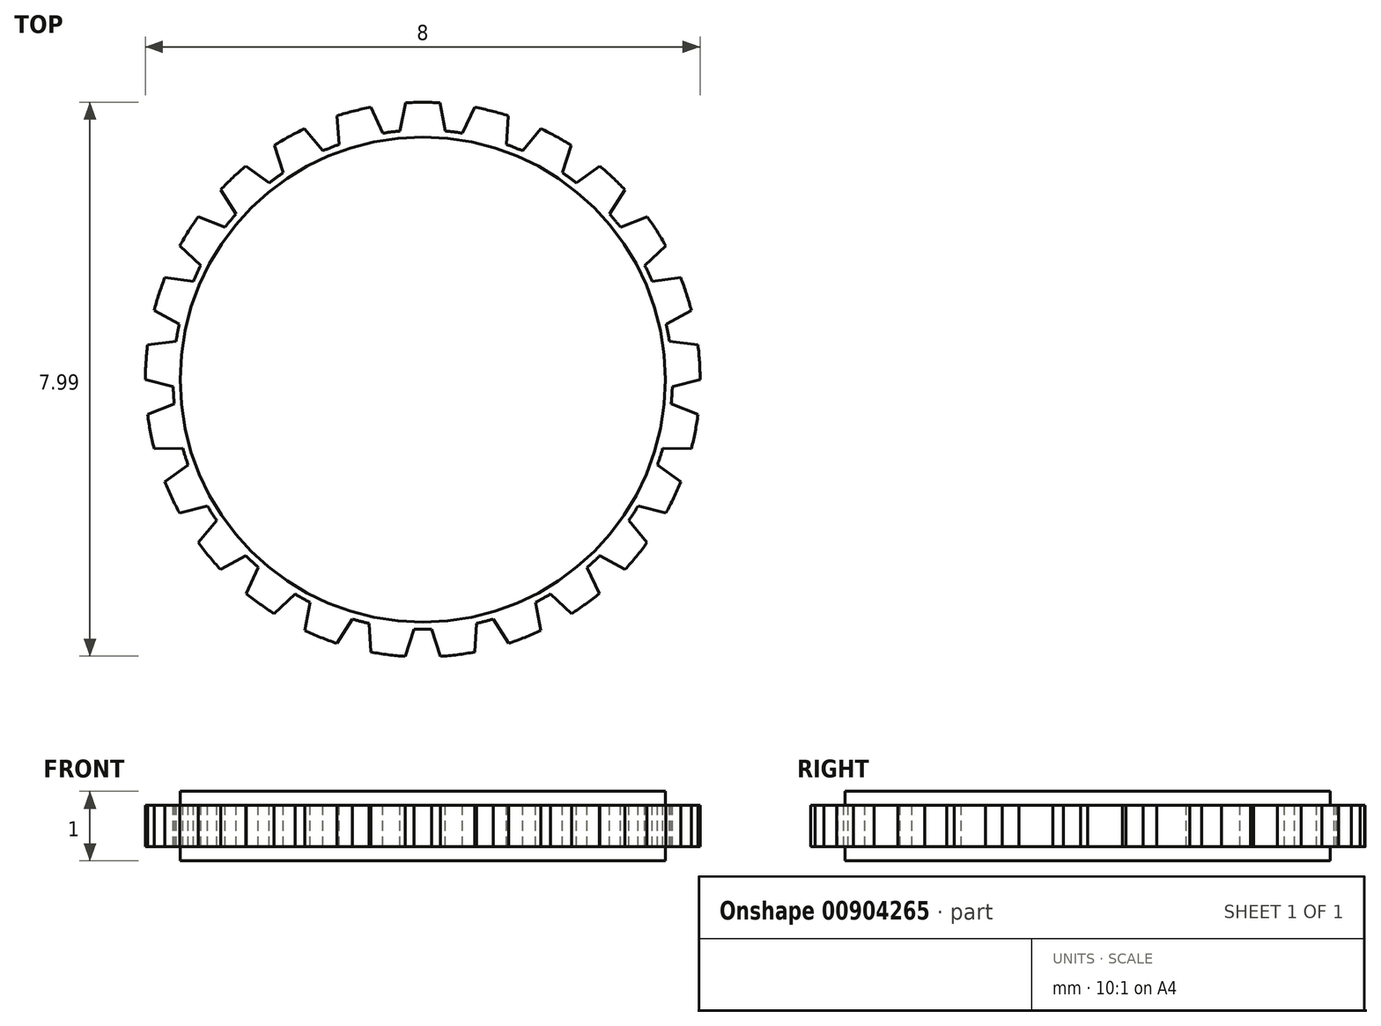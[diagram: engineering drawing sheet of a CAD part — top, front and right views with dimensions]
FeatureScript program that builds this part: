
annotation { "Feature Type Name" : "Feature", "Feature Type Description" : "" }
export const myFeature = defineFeature(function(context is Context, id is Id, definition is map)
    precondition{}
    {
        {
            var Q0;
            Q0=qCreatedBy(makeId("Front.planeOp"),FACE);
            var sketch = newSketch(context, id + "F0", { "sketchPlane" : qUnion([Q0])});
            skLineSegment(sketch, "E0.bottom", {"start": v(0, 0) * mm, "end": v(-4, 0) * mm});
            skLineSegment(sketch, "E0.top", {"start": v(0, 1) * mm, "end": v(-4, 1) * mm});
            skLineSegment(sketch, "E0.left", {"start": v(0, 0) * mm, "end": v(0, 1) * mm});
            skLineSegment(sketch, "E0.right", {"start": v(-4, 0) * mm, "end": v(-4, 1) * mm});
            skLineSegment(sketch, "E1.bottom", {"start": v(0, 1) * mm, "end": v(-1, 1) * mm});
            skLineSegment(sketch, "E1.top", {"start": v(0, 0) * mm, "end": v(-1, 0) * mm});
            skLineSegment(sketch, "E1.left", {"start": v(0, 1) * mm, "end": v(0, 0) * mm});
            skLineSegment(sketch, "E1.right", {"start": v(-1, 1) * mm, "end": v(-1, 0) * mm});
            skSolve(sketch);
        }
        {
            var Q0;
            Q0=makeQuery(id+"F0.imprint","IMPRINT",FACE,{"disambiguationData":[TD([[makeQuery(id+"F0.imprint","IMPRINT",EDGE,{"derivedFrom":sQuery(id+"F0.wireOp",EDGE,"E0.bottom")}),-1.0]])]});
            var Q1;
            Q1=sQuery(id+"F0.wireOp",EDGE,"E1.left");
            revolve(context, id + "F1", {"surfaceOperationType" : NewSurfaceOperationType.NEW, "entities" : qUnion([Q0]), "axis" : qUnion([Q1]), "revolveType" : RevolveType.FULL});
        }
        {
            var Q0;
            Q0=makeQuery(id+"F1.opRevolve","SWEPT_FACE",FACE,{"disambiguationData":[OSD([sQuery(id+"F0.wireOp",EDGE,"E0.top")])]});
            var sketch = newSketch(context, id + "F2", { "sketchPlane" : qUnion([Q0])});
            skLineSegment(sketch, "E2", {"start": v(0, 0) * mm, "end": v(-0.25, 4) * mm});
            skLineSegment(sketch, "E3", {"start": v(0, 0) * mm, "end": v(0.25, 4) * mm});
            skLineSegment(sketch, "E4.1.0", {"start": v(0, 0) * mm, "end": v(-1.23, 3.8) * mm});
            skLineSegment(sketch, "E4.1.1", {"start": v(0, 0) * mm, "end": v(-0.75, 3.93) * mm});
            skLineSegment(sketch, "E4.2.0", {"start": v(0, 0) * mm, "end": v(-2.14, 3.38) * mm});
            skLineSegment(sketch, "E4.2.1", {"start": v(0, 0) * mm, "end": v(-1.7, 3.62) * mm});
            skPoint(sketch, "E4.center", {"position": v(0, 0) * mm});
            skLineSegment(sketch, "E5.2.3.0", {"start": v(0, 0) * mm, "end": v(-2.92, 2.74) * mm});
            skLineSegment(sketch, "E5.3.3.0", {"start": v(0, 0) * mm, "end": v(-2.55, 3.08) * mm});
            skLineSegment(sketch, "E5.2.4.0", {"start": v(0, 0) * mm, "end": v(-3.5, 1.93) * mm});
            skLineSegment(sketch, "E5.3.4.0", {"start": v(0, 0) * mm, "end": v(-3.24, 2.35) * mm});
            skLineSegment(sketch, "E5.2.5.0", {"start": v(0, 0) * mm, "end": v(-3.87, 1) * mm});
            skLineSegment(sketch, "E5.3.5.0", {"start": v(0, 0) * mm, "end": v(-3.72, 1.47) * mm});
            skLineSegment(sketch, "E5.2.6.0", {"start": v(0, 0) * mm, "end": v(-4, 0) * mm});
            skLineSegment(sketch, "E5.3.6.0", {"start": v(0, 0) * mm, "end": v(-3.97, 0.5) * mm});
            skLineSegment(sketch, "E5.2.7.0", {"start": v(0, 0) * mm, "end": v(-3.87, -1) * mm});
            skLineSegment(sketch, "E5.3.7.0", {"start": v(0, 0) * mm, "end": v(-3.97, -0.5) * mm});
            skLineSegment(sketch, "E5.2.8.0", {"start": v(0, 0) * mm, "end": v(-3.5, -1.93) * mm});
            skLineSegment(sketch, "E5.3.8.0", {"start": v(0, 0) * mm, "end": v(-3.72, -1.47) * mm});
            skLineSegment(sketch, "E5.2.9.0", {"start": v(0, 0) * mm, "end": v(-2.92, -2.74) * mm});
            skLineSegment(sketch, "E5.3.9.0", {"start": v(0, 0) * mm, "end": v(-3.24, -2.35) * mm});
            skLineSegment(sketch, "E5.2.10.0", {"start": v(0, 0) * mm, "end": v(-2.14, -3.38) * mm});
            skLineSegment(sketch, "E5.3.10.0", {"start": v(0, 0) * mm, "end": v(-2.55, -3.08) * mm});
            skLineSegment(sketch, "E5.2.11.0", {"start": v(0, 0) * mm, "end": v(-1.24, -3.8) * mm});
            skLineSegment(sketch, "E5.3.11.0", {"start": v(0, 0) * mm, "end": v(-1.7, -3.62) * mm});
            skLineSegment(sketch, "E5.2.12.0", {"start": v(0, 0) * mm, "end": v(-0.25, -4) * mm});
            skLineSegment(sketch, "E5.3.12.0", {"start": v(0, 0) * mm, "end": v(-0.75, -3.93) * mm});
            skLineSegment(sketch, "E5.2.13.0", {"start": v(0, 0) * mm, "end": v(0.75, -3.93) * mm});
            skLineSegment(sketch, "E5.3.13.0", {"start": v(0, 0) * mm, "end": v(0.25, -4) * mm});
            skLineSegment(sketch, "E5.2.14.0", {"start": v(0, 0) * mm, "end": v(1.7, -3.62) * mm});
            skLineSegment(sketch, "E5.3.14.0", {"start": v(0, 0) * mm, "end": v(1.24, -3.8) * mm});
            skLineSegment(sketch, "E6.2.15.0", {"start": v(0, 0) * mm, "end": v(2.55, -3.08) * mm});
            skLineSegment(sketch, "E6.3.15.0", {"start": v(0, 0) * mm, "end": v(2.14, -3.38) * mm});
            skLineSegment(sketch, "E6.2.16.0", {"start": v(0, 0) * mm, "end": v(3.24, -2.35) * mm});
            skLineSegment(sketch, "E6.3.16.0", {"start": v(0, 0) * mm, "end": v(2.92, -2.74) * mm});
            skLineSegment(sketch, "E6.2.17.0", {"start": v(0, 0) * mm, "end": v(3.72, -1.47) * mm});
            skLineSegment(sketch, "E6.3.17.0", {"start": v(0, 0) * mm, "end": v(3.5, -1.93) * mm});
            skLineSegment(sketch, "E6.2.18.0", {"start": v(0, 0) * mm, "end": v(3.97, -0.5) * mm});
            skLineSegment(sketch, "E6.3.18.0", {"start": v(0, 0) * mm, "end": v(3.87, -1) * mm});
            skLineSegment(sketch, "E6.2.19.0", {"start": v(0, 0) * mm, "end": v(3.97, 0.5) * mm});
            skLineSegment(sketch, "E6.3.19.0", {"start": v(0, 0) * mm, "end": v(4, 0) * mm});
            skLineSegment(sketch, "E7.2.20.0", {"start": v(0, 0) * mm, "end": v(3.72, 1.47) * mm});
            skLineSegment(sketch, "E7.3.20.0", {"start": v(0, 0) * mm, "end": v(3.87, 1) * mm});
            skLineSegment(sketch, "E7.2.21.0", {"start": v(0, 0) * mm, "end": v(3.24, 2.35) * mm});
            skLineSegment(sketch, "E7.3.21.0", {"start": v(0, 0) * mm, "end": v(3.5, 1.93) * mm});
            skLineSegment(sketch, "E7.2.22.0", {"start": v(0, 0) * mm, "end": v(2.55, 3.08) * mm});
            skLineSegment(sketch, "E7.3.22.0", {"start": v(0, 0) * mm, "end": v(2.92, 2.74) * mm});
            skLineSegment(sketch, "E7.2.23.0", {"start": v(0, 0) * mm, "end": v(1.7, 3.62) * mm});
            skLineSegment(sketch, "E7.3.23.0", {"start": v(0, 0) * mm, "end": v(2.14, 3.38) * mm});
            skLineSegment(sketch, "E7.2.24.0", {"start": v(0, 0) * mm, "end": v(0.75, 3.93) * mm});
            skLineSegment(sketch, "E7.3.24.0", {"start": v(0, 0) * mm, "end": v(1.23, 3.8) * mm});
            skCircle(sketch, "E8", {"center": v(0, 0) * mm, "radius": 3.6 * mm});
            skLineSegment(sketch, "E9", {"start": v(-1, 0) * mm, "end": v(-0.25, 4) * mm});
            skLineSegment(sketch, "E10", {"start": v(1, 0) * mm, "end": v(0.25, 4) * mm});
            skLineSegment(sketch, "E11.1.0", {"start": v(0.97, 0.25) * mm, "end": v(-0.75, 3.93) * mm});
            skLineSegment(sketch, "E11.1.1", {"start": v(-0.97, -0.25) * mm, "end": v(-1.23, 3.8) * mm});
            skLineSegment(sketch, "E11.2.0", {"start": v(0.88, 0.48) * mm, "end": v(-1.7, 3.62) * mm});
            skLineSegment(sketch, "E11.2.1", {"start": v(-0.88, -0.48) * mm, "end": v(-2.14, 3.38) * mm});
            skLineSegment(sketch, "E12.1.3.0", {"start": v(0.73, 0.68) * mm, "end": v(-2.55, 3.08) * mm});
            skLineSegment(sketch, "E12.3.3.0", {"start": v(-0.73, -0.68) * mm, "end": v(-2.92, 2.74) * mm});
            skLineSegment(sketch, "E12.1.4.0", {"start": v(0.54, 0.84) * mm, "end": v(-3.24, 2.35) * mm});
            skLineSegment(sketch, "E12.3.4.0", {"start": v(-0.54, -0.84) * mm, "end": v(-3.5, 1.93) * mm});
            skLineSegment(sketch, "E12.1.5.0", {"start": v(0.3, 0.95) * mm, "end": v(-3.72, 1.47) * mm});
            skLineSegment(sketch, "E12.3.5.0", {"start": v(-0.3, -0.95) * mm, "end": v(-3.87, 1) * mm});
            skLineSegment(sketch, "E12.1.6.0", {"start": v(0.06, 1) * mm, "end": v(-3.97, 0.5) * mm});
            skLineSegment(sketch, "E12.3.6.0", {"start": v(-0.06, -1) * mm, "end": v(-4, 0) * mm});
            skLineSegment(sketch, "E12.1.7.0", {"start": v(-0.19, 0.98) * mm, "end": v(-3.97, -0.5) * mm});
            skLineSegment(sketch, "E12.3.7.0", {"start": v(0.19, -0.98) * mm, "end": v(-3.87, -1) * mm});
            skLineSegment(sketch, "E12.1.8.0", {"start": v(-0.43, 0.9) * mm, "end": v(-3.72, -1.47) * mm});
            skLineSegment(sketch, "E12.3.8.0", {"start": v(0.43, -0.9) * mm, "end": v(-3.5, -1.93) * mm});
            skLineSegment(sketch, "E12.1.9.0", {"start": v(-0.64, 0.77) * mm, "end": v(-3.24, -2.35) * mm});
            skLineSegment(sketch, "E12.3.9.0", {"start": v(0.64, -0.77) * mm, "end": v(-2.92, -2.74) * mm});
            skLineSegment(sketch, "E12.1.10.0", {"start": v(-0.8, 0.59) * mm, "end": v(-2.55, -3.08) * mm});
            skLineSegment(sketch, "E12.3.10.0", {"start": v(0.8, -0.59) * mm, "end": v(-2.14, -3.38) * mm});
            skLineSegment(sketch, "E12.1.11.0", {"start": v(-0.93, 0.37) * mm, "end": v(-1.7, -3.62) * mm});
            skLineSegment(sketch, "E12.3.11.0", {"start": v(0.93, -0.37) * mm, "end": v(-1.24, -3.8) * mm});
            skLineSegment(sketch, "E12.1.12.0", {"start": v(-1, 0.13) * mm, "end": v(-0.75, -3.93) * mm});
            skLineSegment(sketch, "E12.3.12.0", {"start": v(1, -0.13) * mm, "end": v(-0.25, -4) * mm});
            skLineSegment(sketch, "E12.1.13.0", {"start": v(-1, -0.13) * mm, "end": v(0.25, -4) * mm});
            skLineSegment(sketch, "E12.3.13.0", {"start": v(1, 0.13) * mm, "end": v(0.75, -3.93) * mm});
            skLineSegment(sketch, "E12.1.14.0", {"start": v(-0.93, -0.37) * mm, "end": v(1.24, -3.8) * mm});
            skLineSegment(sketch, "E12.3.14.0", {"start": v(0.93, 0.37) * mm, "end": v(1.7, -3.62) * mm});
            skLineSegment(sketch, "E12.1.15.0", {"start": v(-0.8, -0.59) * mm, "end": v(2.14, -3.38) * mm});
            skLineSegment(sketch, "E12.3.15.0", {"start": v(0.8, 0.59) * mm, "end": v(2.55, -3.08) * mm});
            skLineSegment(sketch, "E12.1.16.0", {"start": v(-0.64, -0.77) * mm, "end": v(2.92, -2.74) * mm});
            skLineSegment(sketch, "E12.3.16.0", {"start": v(0.64, 0.77) * mm, "end": v(3.24, -2.35) * mm});
            skLineSegment(sketch, "E12.1.17.0", {"start": v(-0.43, -0.9) * mm, "end": v(3.5, -1.93) * mm});
            skLineSegment(sketch, "E12.3.17.0", {"start": v(0.43, 0.9) * mm, "end": v(3.72, -1.47) * mm});
            skLineSegment(sketch, "E12.1.18.0", {"start": v(-0.19, -0.98) * mm, "end": v(3.87, -1) * mm});
            skLineSegment(sketch, "E12.3.18.0", {"start": v(0.19, 0.98) * mm, "end": v(3.97, -0.5) * mm});
            skLineSegment(sketch, "E12.1.19.0", {"start": v(0.06, -1) * mm, "end": v(4, 0) * mm});
            skLineSegment(sketch, "E12.3.19.0", {"start": v(-0.06, 1) * mm, "end": v(3.97, 0.5) * mm});
            skLineSegment(sketch, "E12.1.20.0", {"start": v(0.3, -0.95) * mm, "end": v(3.87, 1) * mm});
            skLineSegment(sketch, "E12.3.20.0", {"start": v(-0.3, 0.95) * mm, "end": v(3.72, 1.47) * mm});
            skLineSegment(sketch, "E12.1.21.0", {"start": v(0.54, -0.84) * mm, "end": v(3.5, 1.93) * mm});
            skLineSegment(sketch, "E12.3.21.0", {"start": v(-0.54, 0.84) * mm, "end": v(3.24, 2.35) * mm});
            skLineSegment(sketch, "E12.1.22.0", {"start": v(0.73, -0.68) * mm, "end": v(2.92, 2.74) * mm});
            skLineSegment(sketch, "E12.3.22.0", {"start": v(-0.73, 0.68) * mm, "end": v(2.55, 3.08) * mm});
            skLineSegment(sketch, "E12.1.23.0", {"start": v(0.88, -0.48) * mm, "end": v(2.14, 3.38) * mm});
            skLineSegment(sketch, "E12.3.23.0", {"start": v(-0.88, 0.48) * mm, "end": v(1.7, 3.62) * mm});
            skLineSegment(sketch, "E12.1.24.0", {"start": v(0.97, -0.25) * mm, "end": v(1.23, 3.8) * mm});
            skLineSegment(sketch, "E12.3.24.0", {"start": v(-0.97, 0.25) * mm, "end": v(0.75, 3.93) * mm});
            skSolve(sketch);
        }
        {
            var Q0;
            {var subQ0=sQuery(id+"F2.wireOp",EDGE,"E11.2.1");var subQ1=sQuery(id+"F2.wireOp",EDGE,"E8");var subQ2=makeQuery(id+"F2.imprint","INTERSECT",VERTEX,{"derivedFrom":[subQ1,subQ0]});Q0=makeQuery(id+"F2.imprint","IMPRINT",FACE,{"disambiguationData":[TD([[makeQuery(id+"F2.imprint","IMPRINT",EDGE,{"disambiguationData":[TD([[subQ2,-1.0]])],"derivedFrom":subQ1}),-1.0]])]});}
            var Q1;
            {var subQ0=sQuery(id+"F2.wireOp",EDGE,"E11.1.1");var subQ1=sQuery(id+"F2.wireOp",EDGE,"E8");var subQ2=makeQuery(id+"F2.imprint","INTERSECT",VERTEX,{"derivedFrom":[subQ1,subQ0]});Q1=makeQuery(id+"F2.imprint","IMPRINT",FACE,{"disambiguationData":[TD([[makeQuery(id+"F2.imprint","IMPRINT",EDGE,{"disambiguationData":[TD([[subQ2,-1.0]])],"derivedFrom":subQ1}),-1.0]])]});}
            var Q2;
            {var subQ0=sQuery(id+"F2.wireOp",EDGE,"E9");var subQ1=sQuery(id+"F2.wireOp",EDGE,"E8");var subQ2=makeQuery(id+"F2.imprint","INTERSECT",VERTEX,{"derivedFrom":[subQ1,subQ0]});Q2=makeQuery(id+"F2.imprint","IMPRINT",FACE,{"disambiguationData":[TD([[makeQuery(id+"F2.imprint","IMPRINT",EDGE,{"disambiguationData":[TD([[subQ2,-1.0]])],"derivedFrom":subQ1}),-1.0]])]});}
            var Q3;
            {var subQ0=sQuery(id+"F2.wireOp",EDGE,"E12.3.24.0");var subQ1=sQuery(id+"F2.wireOp",EDGE,"E8");var subQ2=makeQuery(id+"F2.imprint","INTERSECT",VERTEX,{"derivedFrom":[subQ1,subQ0]});Q3=makeQuery(id+"F2.imprint","IMPRINT",FACE,{"disambiguationData":[TD([[makeQuery(id+"F2.imprint","IMPRINT",EDGE,{"disambiguationData":[TD([[subQ2,-1.0]])],"derivedFrom":subQ1}),-1.0]])]});}
            var Q4;
            {var subQ0=sQuery(id+"F2.wireOp",EDGE,"E12.3.23.0");var subQ1=sQuery(id+"F2.wireOp",EDGE,"E8");var subQ2=makeQuery(id+"F2.imprint","INTERSECT",VERTEX,{"derivedFrom":[subQ1,subQ0]});Q4=makeQuery(id+"F2.imprint","IMPRINT",FACE,{"disambiguationData":[TD([[makeQuery(id+"F2.imprint","IMPRINT",EDGE,{"disambiguationData":[TD([[subQ2,-1.0]])],"derivedFrom":subQ1}),-1.0]])]});}
            var Q5;
            {var subQ0=sQuery(id+"F2.wireOp",EDGE,"E12.3.22.0");var subQ1=sQuery(id+"F2.wireOp",EDGE,"E8");var subQ2=makeQuery(id+"F2.imprint","INTERSECT",VERTEX,{"derivedFrom":[subQ1,subQ0]});Q5=makeQuery(id+"F2.imprint","IMPRINT",FACE,{"disambiguationData":[TD([[makeQuery(id+"F2.imprint","IMPRINT",EDGE,{"disambiguationData":[TD([[subQ2,-1.0]])],"derivedFrom":subQ1}),-1.0]])]});}
            var Q6;
            {var subQ0=sQuery(id+"F2.wireOp",EDGE,"E12.3.21.0");var subQ1=sQuery(id+"F2.wireOp",EDGE,"E8");var subQ2=makeQuery(id+"F2.imprint","INTERSECT",VERTEX,{"derivedFrom":[subQ1,subQ0]});Q6=makeQuery(id+"F2.imprint","IMPRINT",FACE,{"disambiguationData":[TD([[makeQuery(id+"F2.imprint","IMPRINT",EDGE,{"disambiguationData":[TD([[subQ2,-1.0]])],"derivedFrom":subQ1}),-1.0]])]});}
            var Q7;
            {var subQ0=sQuery(id+"F2.wireOp",EDGE,"E12.3.20.0");var subQ1=sQuery(id+"F2.wireOp",EDGE,"E8");var subQ2=makeQuery(id+"F2.imprint","INTERSECT",VERTEX,{"derivedFrom":[subQ1,subQ0]});Q7=makeQuery(id+"F2.imprint","IMPRINT",FACE,{"disambiguationData":[TD([[makeQuery(id+"F2.imprint","IMPRINT",EDGE,{"disambiguationData":[TD([[subQ2,-1.0]])],"derivedFrom":subQ1}),-1.0]])]});}
            var Q8;
            {var subQ0=sQuery(id+"F2.wireOp",EDGE,"E12.3.19.0");var subQ1=sQuery(id+"F2.wireOp",EDGE,"E8");var subQ2=makeQuery(id+"F2.imprint","INTERSECT",VERTEX,{"derivedFrom":[subQ1,subQ0]});Q8=makeQuery(id+"F2.imprint","IMPRINT",FACE,{"disambiguationData":[TD([[makeQuery(id+"F2.imprint","IMPRINT",EDGE,{"disambiguationData":[TD([[subQ2,-1.0]])],"derivedFrom":subQ1}),-1.0]])]});}
            var Q9;
            {var subQ0=sQuery(id+"F2.wireOp",EDGE,"E12.3.18.0");var subQ1=sQuery(id+"F2.wireOp",EDGE,"E8");var subQ2=makeQuery(id+"F2.imprint","INTERSECT",VERTEX,{"derivedFrom":[subQ1,subQ0]});Q9=makeQuery(id+"F2.imprint","IMPRINT",FACE,{"disambiguationData":[TD([[makeQuery(id+"F2.imprint","IMPRINT",EDGE,{"disambiguationData":[TD([[subQ2,-1.0]])],"derivedFrom":subQ1}),-1.0]])]});}
            var Q10;
            {var subQ0=sQuery(id+"F2.wireOp",EDGE,"E12.3.17.0");var subQ1=sQuery(id+"F2.wireOp",EDGE,"E8");var subQ2=makeQuery(id+"F2.imprint","INTERSECT",VERTEX,{"derivedFrom":[subQ1,subQ0]});Q10=makeQuery(id+"F2.imprint","IMPRINT",FACE,{"disambiguationData":[TD([[makeQuery(id+"F2.imprint","IMPRINT",EDGE,{"disambiguationData":[TD([[subQ2,-1.0]])],"derivedFrom":subQ1}),-1.0]])]});}
            var Q11;
            {var subQ0=sQuery(id+"F2.wireOp",EDGE,"E12.3.16.0");var subQ1=sQuery(id+"F2.wireOp",EDGE,"E8");var subQ2=makeQuery(id+"F2.imprint","INTERSECT",VERTEX,{"derivedFrom":[subQ1,subQ0]});Q11=makeQuery(id+"F2.imprint","IMPRINT",FACE,{"disambiguationData":[TD([[makeQuery(id+"F2.imprint","IMPRINT",EDGE,{"disambiguationData":[TD([[subQ2,-1.0]])],"derivedFrom":subQ1}),-1.0]])]});}
            var Q12;
            {var subQ0=sQuery(id+"F2.wireOp",EDGE,"E12.3.15.0");var subQ1=sQuery(id+"F2.wireOp",EDGE,"E8");var subQ2=makeQuery(id+"F2.imprint","INTERSECT",VERTEX,{"derivedFrom":[subQ1,subQ0]});Q12=makeQuery(id+"F2.imprint","IMPRINT",FACE,{"disambiguationData":[TD([[makeQuery(id+"F2.imprint","IMPRINT",EDGE,{"disambiguationData":[TD([[subQ2,-1.0]])],"derivedFrom":subQ1}),-1.0]])]});}
            var Q13;
            {var subQ0=sQuery(id+"F2.wireOp",EDGE,"E12.3.14.0");var subQ1=sQuery(id+"F2.wireOp",EDGE,"E8");var subQ2=makeQuery(id+"F2.imprint","INTERSECT",VERTEX,{"derivedFrom":[subQ1,subQ0]});Q13=makeQuery(id+"F2.imprint","IMPRINT",FACE,{"disambiguationData":[TD([[makeQuery(id+"F2.imprint","IMPRINT",EDGE,{"disambiguationData":[TD([[subQ2,-1.0]])],"derivedFrom":subQ1}),-1.0]])]});}
            var Q14;
            {var subQ0=sQuery(id+"F2.wireOp",EDGE,"E12.3.13.0");var subQ1=sQuery(id+"F2.wireOp",EDGE,"E8");var subQ2=makeQuery(id+"F2.imprint","INTERSECT",VERTEX,{"derivedFrom":[subQ1,subQ0]});Q14=makeQuery(id+"F2.imprint","IMPRINT",FACE,{"disambiguationData":[TD([[makeQuery(id+"F2.imprint","IMPRINT",EDGE,{"disambiguationData":[TD([[subQ2,-1.0]])],"derivedFrom":subQ1}),-1.0]])]});}
            var Q15;
            {var subQ0=sQuery(id+"F2.wireOp",EDGE,"E12.3.12.0");var subQ1=sQuery(id+"F2.wireOp",EDGE,"E8");var subQ2=makeQuery(id+"F2.imprint","INTERSECT",VERTEX,{"derivedFrom":[subQ1,subQ0]});Q15=makeQuery(id+"F2.imprint","IMPRINT",FACE,{"disambiguationData":[TD([[makeQuery(id+"F2.imprint","IMPRINT",EDGE,{"disambiguationData":[TD([[subQ2,-1.0]])],"derivedFrom":subQ1}),-1.0]])]});}
            var Q16;
            {var subQ0=sQuery(id+"F2.wireOp",EDGE,"E12.3.11.0");var subQ1=sQuery(id+"F2.wireOp",EDGE,"E8");var subQ2=makeQuery(id+"F2.imprint","INTERSECT",VERTEX,{"derivedFrom":[subQ1,subQ0]});Q16=makeQuery(id+"F2.imprint","IMPRINT",FACE,{"disambiguationData":[TD([[makeQuery(id+"F2.imprint","IMPRINT",EDGE,{"disambiguationData":[TD([[subQ2,-1.0]])],"derivedFrom":subQ1}),-1.0]])]});}
            var Q17;
            {var subQ0=sQuery(id+"F2.wireOp",EDGE,"E12.3.10.0");var subQ1=sQuery(id+"F2.wireOp",EDGE,"E8");var subQ2=makeQuery(id+"F2.imprint","INTERSECT",VERTEX,{"derivedFrom":[subQ1,subQ0]});Q17=makeQuery(id+"F2.imprint","IMPRINT",FACE,{"disambiguationData":[TD([[makeQuery(id+"F2.imprint","IMPRINT",EDGE,{"disambiguationData":[TD([[subQ2,-1.0]])],"derivedFrom":subQ1}),-1.0]])]});}
            var Q18;
            {var subQ0=sQuery(id+"F2.wireOp",EDGE,"E12.3.8.0");var subQ1=sQuery(id+"F2.wireOp",EDGE,"E8");var subQ2=makeQuery(id+"F2.imprint","INTERSECT",VERTEX,{"derivedFrom":[subQ1,subQ0]});Q18=makeQuery(id+"F2.imprint","IMPRINT",FACE,{"disambiguationData":[TD([[makeQuery(id+"F2.imprint","IMPRINT",EDGE,{"disambiguationData":[TD([[subQ2,-1.0]])],"derivedFrom":subQ1}),-1.0]])]});}
            var Q19;
            {var subQ0=sQuery(id+"F2.wireOp",EDGE,"E12.3.9.0");var subQ1=sQuery(id+"F2.wireOp",EDGE,"E8");var subQ2=makeQuery(id+"F2.imprint","INTERSECT",VERTEX,{"derivedFrom":[subQ1,subQ0]});Q19=makeQuery(id+"F2.imprint","IMPRINT",FACE,{"disambiguationData":[TD([[makeQuery(id+"F2.imprint","IMPRINT",EDGE,{"disambiguationData":[TD([[subQ2,-1.0]])],"derivedFrom":subQ1}),-1.0]])]});}
            var Q20;
            {var subQ0=sQuery(id+"F2.wireOp",EDGE,"E12.3.7.0");var subQ1=sQuery(id+"F2.wireOp",EDGE,"E8");var subQ2=makeQuery(id+"F2.imprint","INTERSECT",VERTEX,{"derivedFrom":[subQ1,subQ0]});Q20=makeQuery(id+"F2.imprint","IMPRINT",FACE,{"disambiguationData":[TD([[makeQuery(id+"F2.imprint","IMPRINT",EDGE,{"disambiguationData":[TD([[subQ2,-1.0]])],"derivedFrom":subQ1}),-1.0]])]});}
            var Q21;
            {var subQ0=sQuery(id+"F2.wireOp",EDGE,"E12.3.6.0");var subQ1=sQuery(id+"F2.wireOp",EDGE,"E8");var subQ2=makeQuery(id+"F2.imprint","INTERSECT",VERTEX,{"derivedFrom":[subQ1,subQ0]});Q21=makeQuery(id+"F2.imprint","IMPRINT",FACE,{"disambiguationData":[TD([[makeQuery(id+"F2.imprint","IMPRINT",EDGE,{"disambiguationData":[TD([[subQ2,-1.0]])],"derivedFrom":subQ1}),-1.0]])]});}
            var Q22;
            {var subQ0=sQuery(id+"F2.wireOp",EDGE,"E12.3.5.0");var subQ1=sQuery(id+"F2.wireOp",EDGE,"E8");var subQ2=makeQuery(id+"F2.imprint","INTERSECT",VERTEX,{"derivedFrom":[subQ1,subQ0]});Q22=makeQuery(id+"F2.imprint","IMPRINT",FACE,{"disambiguationData":[TD([[makeQuery(id+"F2.imprint","IMPRINT",EDGE,{"disambiguationData":[TD([[subQ2,-1.0]])],"derivedFrom":subQ1}),-1.0]])]});}
            var Q23;
            {var subQ0=sQuery(id+"F2.wireOp",EDGE,"E12.3.4.0");var subQ1=sQuery(id+"F2.wireOp",EDGE,"E8");var subQ2=makeQuery(id+"F2.imprint","INTERSECT",VERTEX,{"derivedFrom":[subQ1,subQ0]});Q23=makeQuery(id+"F2.imprint","IMPRINT",FACE,{"disambiguationData":[TD([[makeQuery(id+"F2.imprint","IMPRINT",EDGE,{"disambiguationData":[TD([[subQ2,-1.0]])],"derivedFrom":subQ1}),-1.0]])]});}
            var Q24;
            {var subQ0=sQuery(id+"F2.wireOp",EDGE,"E12.3.3.0");var subQ1=sQuery(id+"F2.wireOp",EDGE,"E8");var subQ2=makeQuery(id+"F2.imprint","INTERSECT",VERTEX,{"derivedFrom":[subQ1,subQ0]});Q24=makeQuery(id+"F2.imprint","IMPRINT",FACE,{"disambiguationData":[TD([[makeQuery(id+"F2.imprint","IMPRINT",EDGE,{"disambiguationData":[TD([[subQ2,-1.0]])],"derivedFrom":subQ1}),-1.0]])]});}
            extrude(context, id + "F3", {"entities" : qUnion([Q0, Q1, Q2, Q3, Q4, Q5, Q6, Q7, Q8, Q9, Q10, Q11, Q12, Q13, Q14, Q15, Q16, Q17, Q18, Q19, Q20, Q21, Q22, Q23, Q24]), "operationType" : NewBodyOperationType.REMOVE, "oppositeDirection" : true, "depth" : 25 * mm, "offsetDistance" : 25 * mm});
        }
        {
            var Q0;
            Q0=makeQuery(id+"F1.opRevolve","SWEPT_FACE",FACE,{"disambiguationData":[OSD([sQuery(id+"F0.wireOp",EDGE,"E0.top")])]});
            var sketch = newSketch(context, id + "F4", { "sketchPlane" : qUnion([Q0])});
            skCircle(sketch, "E13", {"center": v(0, 0) * mm, "radius": 3.5 * mm});
            skSolve(sketch);
        }
        {
            var Q0;
            Q0=makeQuery(id+"F1.opRevolve","SWEPT_FACE",FACE,{"disambiguationData":[OSD([sQuery(id+"F0.wireOp",EDGE,"E0.bottom")])]});
            var sketch = newSketch(context, id + "F5", { "sketchPlane" : qUnion([Q0])});
            skCircle(sketch, "E14", {"center": v(0, 0) * mm, "radius": 3.5 * mm});
            skSolve(sketch);
        }
        {
            var Q0;
            Q0=makeQuery(id+"F5.imprint","IMPRINT",FACE,{"disambiguationData":[TD([[makeQuery(id+"F5.imprint","IMPRINT",EDGE,{"derivedFrom":sQuery(id+"F5.wireOp",EDGE,"E14")}),-1.0]])]});
            extrude(context, id + "F6", {"entities" : qUnion([Q0]), "operationType" : NewBodyOperationType.REMOVE, "oppositeDirection" : true, "depth" : 0.2 * mm, "offsetDistance" : 25 * mm});
        }
        {
            var Q0;
            Q0=makeQuery(id+"F4.imprint","IMPRINT",FACE,{"disambiguationData":[TD([[makeQuery(id+"F4.imprint","IMPRINT",EDGE,{"derivedFrom":sQuery(id+"F4.wireOp",EDGE,"E13")}),-1.0]])]});
            extrude(context, id + "F7", {"entities" : qUnion([Q0]), "operationType" : NewBodyOperationType.REMOVE, "oppositeDirection" : true, "depth" : 0.2 * mm, "offsetDistance" : 25 * mm});
        }
    });
